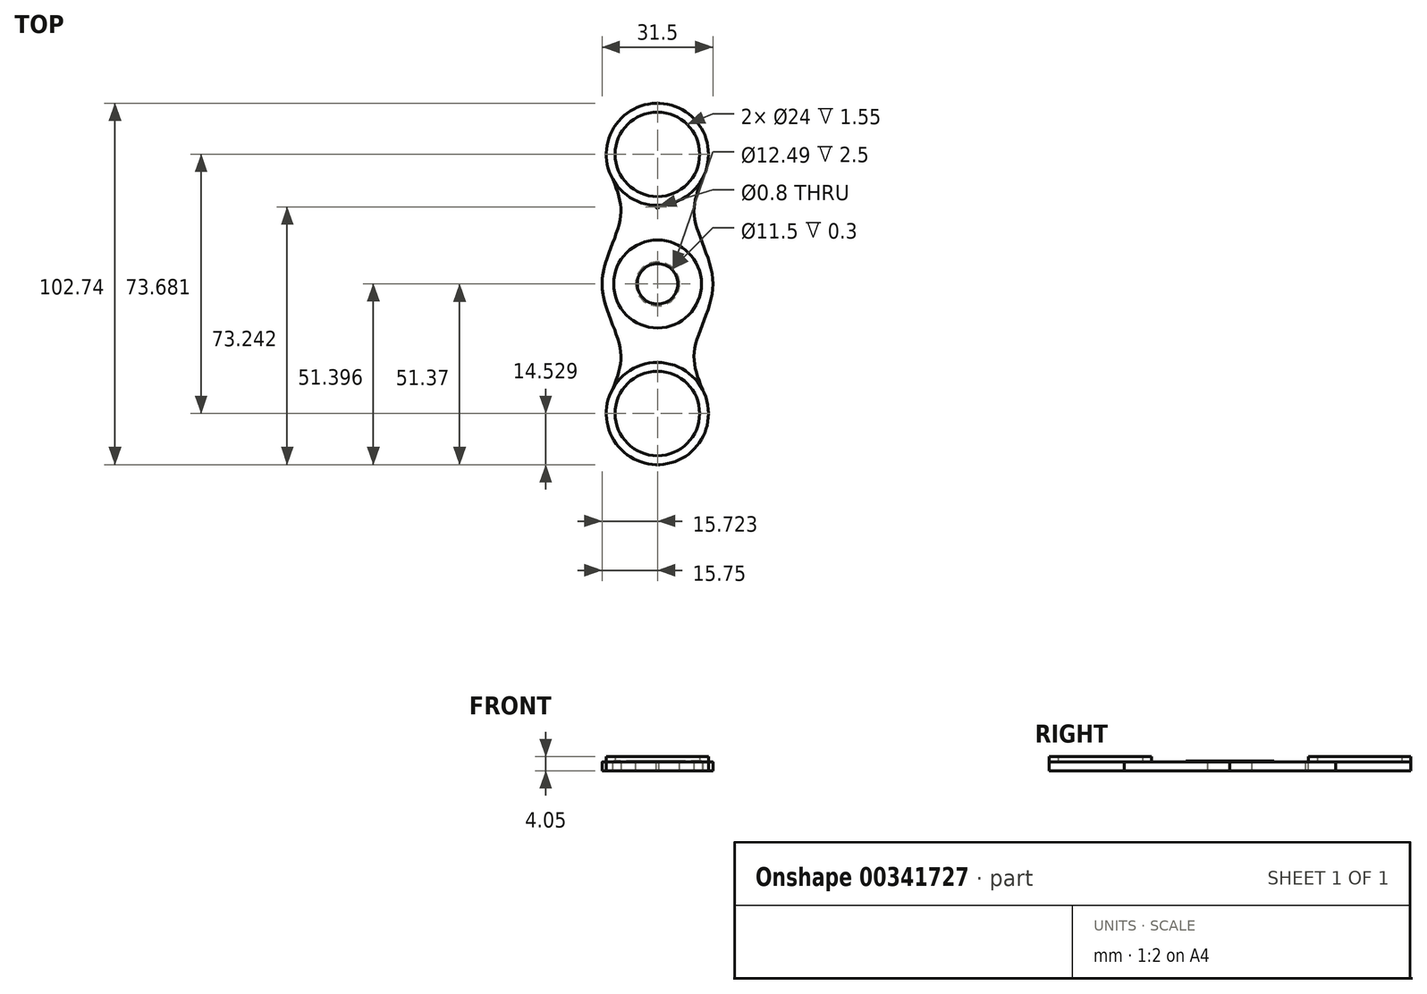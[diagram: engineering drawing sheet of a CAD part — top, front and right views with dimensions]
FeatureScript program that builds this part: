
annotation { "Feature Type Name" : "Feature", "Feature Type Description" : "" }
export const myFeature = defineFeature(function(context is Context, id is Id, definition is map)
    precondition{}
    {
        {
            var Q0;
            Q0=qCreatedBy(makeId("Top.planeOp"),FACE);
            var sketch = newSketch(context, id + "F0", { "sketchPlane" : qUnion([Q0])});
            skCircle(sketch, "E0", {"center": v(-0.03, 36.84) * mm, "radius": 14.5 * mm});
            skPoint(sketch, "E0.first.point", {"position": v(-14.52, 37.09) * mm});
            skPoint(sketch, "E0.second.point", {"position": v(14.47, 36.66) * mm});
            skPoint(sketch, "E0.third.point", {"position": v(0, 22.34) * mm});
            skSolve(sketch);
        }
        {
            var Q0;
            Q0=makeQuery(id+"F0.imprint","IMPRINT",FACE,{"disambiguationData":[TD([[makeQuery(id+"F0.imprint","IMPRINT",EDGE,{"derivedFrom":sQuery(id+"F0.wireOp",EDGE,"E0")}),1.0]])]});
            extrude(context, id + "F1", {"entities" : qUnion([Q0]), "depth" : 2.5 * mm});
        }
        {
            var Q0;
            Q0=makeQuery(id+"F1.opExtrude","SWEPT_BODY",BODY,{"disambiguationData":[OSD([sQuery(id+"F0.wireOp",EDGE,"E0")])]});
            var Q1;
            Q1=makeQuery(id+"F1.opExtrude","CAP_FACE",FACE,{"disambiguationData":[OSD([sQuery(id+"F0.wireOp",EDGE,"E0")])],"isStart":false});
            var Q2;
            Q2=qCreatedBy(makeId("Front.planeOp"),FACE);
            mirror(context, id + "F2", {"operationType" : NewBodyOperationType.ADD, "entities" : qUnion([Q0]), "faces" : qUnion([Q1]), "mirrorPlane" : qUnion([Q2])});
        }
        {
            var Q0;
            Q0=qCreatedBy(makeId("Top.planeOp"),FACE);
            var sketch = newSketch(context, id + "F3", { "sketchPlane" : qUnion([Q0])});
            skFitSpline(sketch, "E1", {"points": [v(-12.09, 28.75) * mm, v(-10.3, 16.8) * mm, v(-15.75, 0) * mm, v(-10.67, -17.86) * mm, v(-12.82, -30.03) * mm], "startDerivative": vector(31.75, -58.25) * mm, "endDerivative": vector(-25.02, -61.58) * mm});
            skFitSpline(sketch, "E2.MirrorCS", {"points": [v(12.09, 28.75) * mm, v(10.3, 16.8) * mm, v(15.75, 0) * mm, v(10.67, -17.86) * mm, v(12.82, -30.03) * mm], "startDerivative": vector(-31.75, -58.25) * mm, "endDerivative": vector(25.02, -61.58) * mm});
            skLineSegment(sketch, "E3", {"start": v(-12.09, 28.75) * mm, "end": v(12.09, 28.75) * mm});
            skLineSegment(sketch, "E4", {"start": v(-12.82, -30.03) * mm, "end": v(12.82, -30.03) * mm});
            skSolve(sketch);
        }
        {
            var Q0;
            Q0=makeQuery(id+"F3.imprint","IMPRINT",FACE,{"disambiguationData":[TD([[makeQuery(id+"F3.imprint","IMPRINT",EDGE,{"derivedFrom":sQuery(id+"F3.wireOp",EDGE,"E1")}),1.0]])]});
            extrude(context, id + "F4", {"entities" : qUnion([Q0]), "operationType" : NewBodyOperationType.ADD, "depth" : 2.5 * mm});
        }
        {
            var Q0;
            {var subQ0=makeQuery(id+"F1.opExtrude","CAP_FACE",FACE,{"disambiguationData":[OSD([sQuery(id+"F0.wireOp",EDGE,"E0")])],"isStart":false});Q0=makeQuery(id+"F4.boolean.opBoolean","MERGE",FACE,{"derivedFrom":[subQ0,makeQuery(id+"F2.opPattern","COPY",FACE,{"derivedFrom":subQ0,"instanceName":"1"}),makeQuery(id+"F4.opExtrude","CAP_FACE",FACE,{"disambiguationData":[OSD([sQuery(id+"F3.wireOp",EDGE,"E1"),sQuery(id+"F3.wireOp",EDGE,"E2.MirrorCS"),sQuery(id+"F3.wireOp",EDGE,"E3"),sQuery(id+"F3.wireOp",EDGE,"E4")])],"isStart":false})]});}
            var sketch = newSketch(context, id + "F5", { "sketchPlane" : qUnion([Q0])});
            skCircle(sketch, "E5", {"center": v(-0.03, 36.84) * mm, "radius": 14.52 * mm});
            skCircle(sketch, "E6", {"center": v(-0.03, -36.84) * mm, "radius": 14.5 * mm});
            skSolve(sketch);
        }
        {
            var Q0;
            Q0 = qSketchRegion(id + "F5", true);
            extrude(context, id + "F6", {"entities" : qUnion([Q0]), "operationType" : NewBodyOperationType.ADD, "depth" : 1.55 * mm});
        }
        {
            var Q0;
            Q0=makeQuery(id+"F6.opExtrude","CAP_FACE",FACE,{"disambiguationData":[OSD([sQuery(id+"F5.wireOp",EDGE,"E5")])],"isStart":false});
            var Q1;
            Q1=makeQuery(id+"F6.opExtrude","CAP_FACE",FACE,{"disambiguationData":[OSD([sQuery(id+"F5.wireOp",EDGE,"E6")])],"isStart":false});
            shell(context, id + "F7", {"entities" : qUnion([Q0, Q1]), "thickness" : 2.5 * mm});
        }
        {
            var Q0;
            Q0=makeQuery(id+"F6.opExtrude","CAP_FACE",FACE,{"disambiguationData":[OSD([sQuery(id+"F5.wireOp",EDGE,"E6")])],"isStart":false});
            shell(context, id + "F8", {"entities" : qUnion([Q0]), "thickness" : 2.5 * mm});
        }
        {
            var Q0;
            Q0 = qSketchRegion(id + "F5", true);
            var sketch = newSketch(context, id + "F9", { "sketchPlane" : qUnion([Q0])});
            skSolve(sketch);
        }
        {
            var Q0;
            Q0=makeQuery(id+"F5.imprint","IMPRINT",FACE,{"disambiguationData":[TD([[makeQuery(id+"F5.imprint","IMPRINT",EDGE,{"disambiguationData":[OD(0.0)],"derivedFrom":sQuery(id+"F5.wireOp",EDGE,"E6")}),-1.0]])]});
            var sketch = newSketch(context, id + "F10", { "sketchPlane" : qUnion([Q0])});
            skLineSegment(sketch, "E7.bottom", {"start": v(6.67, 23.56) * mm, "end": v(-5.88, 23.56) * mm});
            skLineSegment(sketch, "E7.top", {"start": v(6.67, 21.32) * mm, "end": v(-5.88, 21.32) * mm});
            skLineSegment(sketch, "E7.left", {"start": v(6.67, 23.56) * mm, "end": v(6.67, 21.32) * mm});
            skLineSegment(sketch, "E7.right", {"start": v(-5.88, 23.56) * mm, "end": v(-5.88, 21.32) * mm});
            skSolve(sketch);
        }
        {
            var Q0;
            Q0=makeQuery(id+"F1.opExtrude","SWEPT_BODY",BODY,{"disambiguationData":[OSD([sQuery(id+"F0.wireOp",EDGE,"E0")])]});
            var Q1;
            Q1=qCreatedBy(makeId("Front.planeOp"),FACE);
            mirror(context, id + "F11", {"operationType" : NewBodyOperationType.ADD, "entities" : qUnion([Q0]), "mirrorPlane" : qUnion([Q1])});
        }
        {
            var Q0;
            Q0=makeQuery(id+"F5.imprint","IMPRINT",FACE,{"disambiguationData":[TD([[makeQuery(id+"F5.imprint","IMPRINT",EDGE,{"disambiguationData":[OD(0.0)],"derivedFrom":sQuery(id+"F5.wireOp",EDGE,"E6")}),-1.0]])]});
            var sketch = newSketch(context, id + "F12", { "sketchPlane" : qUnion([Q0])});
            skCircle(sketch, "E8", {"center": v(0, 0) * mm, "radius": 12.5 * mm});
            skSolve(sketch);
        }
        {
            var Q0;
            Q0 = qSketchRegion(id + "F12", true);
            var sketch = newSketch(context, id + "F13", { "sketchPlane" : qUnion([Q0])});
            skCircle(sketch, "E9", {"center": v(0.02, 0) * mm, "radius": 12.49 * mm});
            skPoint(sketch, "E9.first.point", {"position": v(-8.63, 9) * mm});
            skPoint(sketch, "E9.second.point", {"position": v(-6.8, -10.46) * mm});
            skPoint(sketch, "E9.third.point", {"position": v(12.49, 0.65) * mm});
            skSolve(sketch);
        }
        {
            var Q0;
            Q0=sQuery(id+"F12.wireOp",VERTEX,"E8.center");
            var Q1;
            Q1=makeQuery(id+"F1.opExtrude","SWEPT_BODY",BODY,{"disambiguationData":[OSD([sQuery(id+"F0.wireOp",EDGE,"E0")])]});
            hole(context, id + "F14", {"style" : HoleStyle.SIMPLE, "endStyle" : HoleEndStyle.THROUGH, "holeDiameter" : 12.5 * mm, "isTappedThrough" : true, "tappedDepth" : 12 * mm, "tapClearance" : 3, "locations" : qUnion([Q0]), "scope" : qUnion([Q1])});
        }
        {
            var Q0;
            {var subQ24=sQuery(id+"F10.wireOp",EDGE,"E7.top");Q0=makeQuery(id+"F10.imprint","IMPRINT",FACE,{"disambiguationData":[TD([[makeQuery(id+"F10.imprint","IMPRINT",EDGE,{"derivedFrom":subQ24}),1.0]])]});}
            var sketch = newSketch(context, id + "F15", { "sketchPlane" : qUnion([Q0])});
            skPoint(sketch, "E10", {"position": v(0, 0.03) * mm});
            skPoint(sketch, "E11", {"position": v(0, 12.52) * mm});
            skSolve(sketch);
        }
        {
            var Q0;
            {var subQ1=sQuery(id+"F10.wireOp",EDGE,"E7.top");Q0=makeQuery(id+"F10.imprint","IMPRINT",FACE,{"disambiguationData":[TD([[makeQuery(id+"F10.imprint","IMPRINT",EDGE,{"derivedFrom":subQ1}),-1.0]])]});}
            var sketch = newSketch(context, id + "F16", { "sketchPlane" : qUnion([Q0])});
            skPoint(sketch, "E12", {"position": v(0, 21.87) * mm});
            skSolve(sketch);
        }
        {
            var Q0;
            Q0=sQuery(id+"F16.wireOp",VERTEX,"E12");
            var Q1;
            Q1=makeQuery(id+"F1.opExtrude","SWEPT_BODY",BODY,{"disambiguationData":[OSD([sQuery(id+"F0.wireOp",EDGE,"E0")])]});
            hole(context, id + "F17", {"style" : HoleStyle.SIMPLE, "endStyle" : HoleEndStyle.THROUGH, "holeDiameter" : .8 * mm, "isTappedThrough" : true, "tappedDepth" : 12 * mm, "tapClearance" : 3, "locations" : qUnion([Q0]), "scope" : qUnion([Q1])});
        }
        {
            var Q0;
            Q0=makeQuery(id+"F5.imprint","IMPRINT",FACE,{"disambiguationData":[TD([[makeQuery(id+"F5.imprint","IMPRINT",EDGE,{"disambiguationData":[OD(0.0)],"derivedFrom":sQuery(id+"F5.wireOp",EDGE,"E6")}),-1.0]])]});
            var sketch = newSketch(context, id + "F18", { "sketchPlane" : qUnion([Q0])});
            skPoint(sketch, "E13", {"position": v(0, -21.87) * mm});
            skCircle(sketch, "E14", {"center": v(0, -21.87) * mm, "radius": 0.45 * mm});
            skPoint(sketch, "E15", {"position": v(0.44, -21.88) * mm});
            skSolve(sketch);
        }
        {
            var Q0;
            Q0 = qSketchRegion(id + "F13", true);
            extrude(context, id + "F19", {"entities" : qUnion([Q0]), "operationType" : NewBodyOperationType.ADD, "depth" : .3 * mm});
        }
        {
            var Q0;
            Q0=sQuery(id+"F15.wireOp",VERTEX,"E10");
            var Q1;
            Q1=makeQuery(id+"F1.opExtrude","SWEPT_BODY",BODY,{"disambiguationData":[OSD([sQuery(id+"F0.wireOp",EDGE,"E0")])]});
            hole(context, id + "F20", {"style" : HoleStyle.SIMPLE, "endStyle" : HoleEndStyle.THROUGH, "oppositeDirection" : true, "holeDiameter" : 11.5 * mm, "isTappedThrough" : true, "tappedDepth" : 12 * mm, "tapClearance" : 3, "locations" : qUnion([Q0]), "scope" : qUnion([Q1])});
        }
    });
